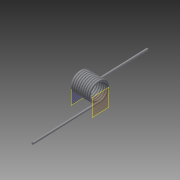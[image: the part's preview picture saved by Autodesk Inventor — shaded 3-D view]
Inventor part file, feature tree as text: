
AUTODESK INVENTOR PART (.ipt)
format: ipt  version: 2014 (Build 180170000, 170)  size: 282,112 bytes
history: native  units: in
note: dims shown in document units (in); Inventor stores cm internally (conversion verified against a paired STEP export)
features: other x2, plane x2, imported_body x1
ambient origin geometry x8: Origin, YZ Plane, XZ Plane, XY Plane, X Axis, Y Axis, Z Axis, Center Point
bodies: Body1 (feature_tree)
feature tree (5):
  parser-record x1  (decoder bookkeeping rows leaked as tree rows — omitted from the tree; the rows remain in map.json)
  other  "9271K6251"
  plane  "Work Plane1"
  plane  "Work Plane2"
  imported_body  "Base1"
